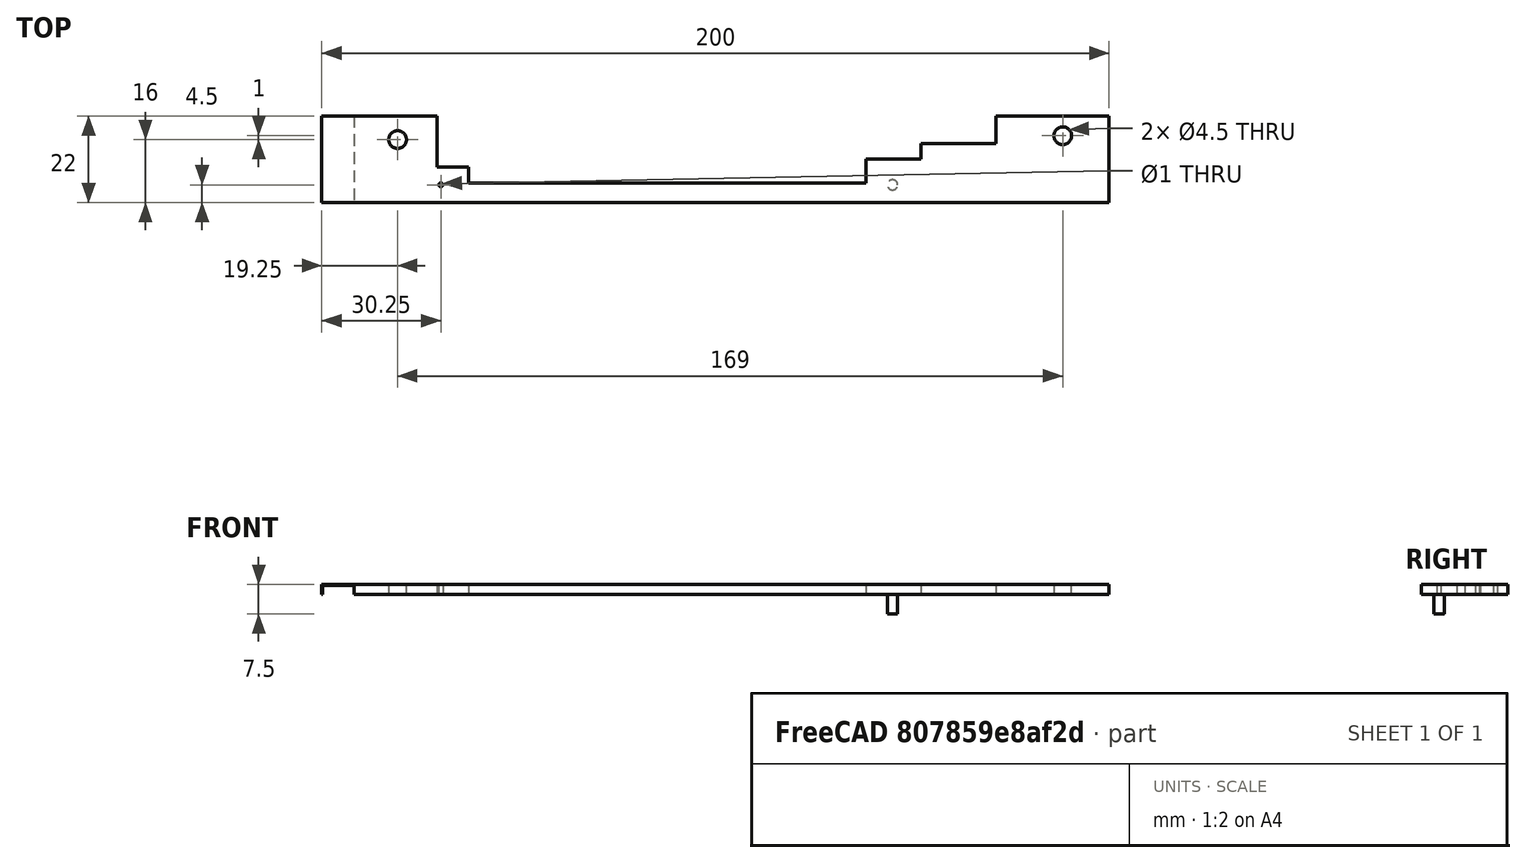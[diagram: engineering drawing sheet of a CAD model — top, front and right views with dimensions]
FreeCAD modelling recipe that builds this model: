
FCSTD DOCUMENT  (FreeCAD 0.21R33668 +26 (Git))
Label: 4-vector-support-lf
License: All rights reserved
LicenseURL: http://en.wikipedia.org/wiki/All_rights_reserved
objects: PartDesign::SubtractiveBox×5, PartDesign::SubtractiveCylinder×3, PartDesign::AdditiveBox×1, PartDesign::AdditiveCylinder×1, PartDesign::Body×1
note: 21 computed .brp shape members not serialized (recipe doc carries the construction recipe); baked Part::Feature solids carry a one-line shape summary decoded from their .brp

FEATURE [PartDesign::AdditiveBox] Box  label="bar-1"
  AttacherType = Attacher::AttachEngine3D
  Height = 2.5
  Length = 200
  Width = 22
FEATURE [PartDesign::SubtractiveCylinder] Cylinder  label="mp1"
  Angle = 360
  AttacherType = Attacher::AttachEngine3D
  AttachmentOffset = pos=(19.25,16,-2.5) rot=(0,0,1;0rad)
  BaseFeature = -> Box
  FirstAngle = 0
  Height = 2.5
  MapMode = 5
  Placement = pos=(19.25,16,0) rot=(0,0,1;0rad)
  Radius = 2.25
  SecondAngle = 0
  Support = -> [Box]
FEATURE [PartDesign::SubtractiveCylinder] Cylinder001  label="mp2"
  Angle = 360
  AttacherType = Attacher::AttachEngine3D
  AttachmentOffset = pos=(169,1,-2.5) rot=(0,0,1;0rad)
  BaseFeature = -> Cylinder
  FirstAngle = 0
  Height = 2.5
  MapMode = 5
  Placement = pos=(188.25,17,0) rot=(0,0,1;0rad)
  Radius = 2.25
  SecondAngle = 0
  Support = -> [Cylinder]
FEATURE [PartDesign::AdditiveCylinder] Cylinder003  label="mount-lg"
  Angle = 360
  AttacherType = Attacher::AttachEngine3D
  AttachmentOffset = pos=(103.5,-4.5,-5) rot=(0,0,1;0rad)
  BaseFeature = -> Cylinder001
  FirstAngle = 0
  Height = 6
  MapMode = 2
  Placement = pos=(145,4.5,-5) rot=(0,0,1;0rad)
  Radius = 1.3
  SecondAngle = 0
FEATURE [PartDesign::SubtractiveCylinder] Cylinder004  label="negative-mount-sm"
  Angle = 360
  AttacherType = Attacher::AttachEngine3D
  AttachmentOffset = pos=(-114.75,0,-2.5) rot=(0,0,1;0rad)
  BaseFeature = -> Cylinder003
  FirstAngle = 0
  Height = 2.5
  MapMode = 5
  Placement = pos=(30.25,4.5,2.5) rot=(1,0,0;3.14159rad)
  Radius = 0.5
  SecondAngle = 0
  Support = -> [Cylinder003]
FEATURE [PartDesign::SubtractiveBox] Box003  label="negative-trim"
  AttacherType = Attacher::AttachEngine3D
  AttachmentOffset = pos=(-30,-17.5,-2.25) rot=(0,0,1;0rad)
  BaseFeature = -> Cylinder004
  Height = 10
  Length = 8
  MapMode = 5
  Placement = pos=(0.25,22,2.25) rot=(1,0,0;3.14159rad)
  Support = -> [Cylinder004]
  Width = 22
FEATURE [PartDesign::SubtractiveBox] Box004  label="negative-in"
  AttacherType = Attacher::AttachEngine3D
  AttachmentOffset = pos=(37,7,-2.5) rot=(0,0,1;0rad)
  BaseFeature = -> Box003
  Height = 2.5
  Length = 101
  MapMode = 5
  Placement = pos=(37.25,15,2.5) rot=(1,0,0;3.14159rad)
  Support = -> [Box003]
  Width = 10
FEATURE [PartDesign::SubtractiveBox] Box005  label="negative-out"
  AttacherType = Attacher::AttachEngine3D
  AttachmentOffset = pos=(-8,-7,-2.5) rot=(0,0,1;0rad)
  BaseFeature = -> Box004
  Height = 2.5
  Length = 142
  MapMode = 5
  Placement = pos=(29.25,22,2.5) rot=(1,0,0;3.14159rad)
  Support = -> [Box004]
  Width = 7
FEATURE [PartDesign::SubtractiveBox] Box006  label="negative-left"
  AttacherType = Attacher::AttachEngine3D
  AttachmentOffset = pos=(0,7,-2.5) rot=(0,0,1;0rad)
  BaseFeature = -> Box005
  Height = 10
  Length = 8
  MapMode = 5
  Placement = pos=(29.25,15,2.5) rot=(1,0,0;3.14159rad)
  Support = -> [Box005]
  Width = 6
FEATURE [PartDesign::SubtractiveBox] Box007  label="negative-right"
  AttacherType = Attacher::AttachEngine3D
  AttachmentOffset = pos=(109,0,-2.5) rot=(0,0,1;0rad)
  BaseFeature = -> Box006
  Height = 2.5
  Length = 14
  MapMode = 5
  Placement = pos=(138.25,15,2.5) rot=(1,0,0;3.14159rad)
  Support = -> [Box006]
  Width = 4
FEATURE [PartDesign::Body] Body  label="Mount-left"
  Group = -> [Box,Cylinder,Cylinder001,Cylinder003,Cylinder004,Box003,Box004,Box005,Box006,Box007]
  Origin = -> Origin
  Tip = -> Box007
